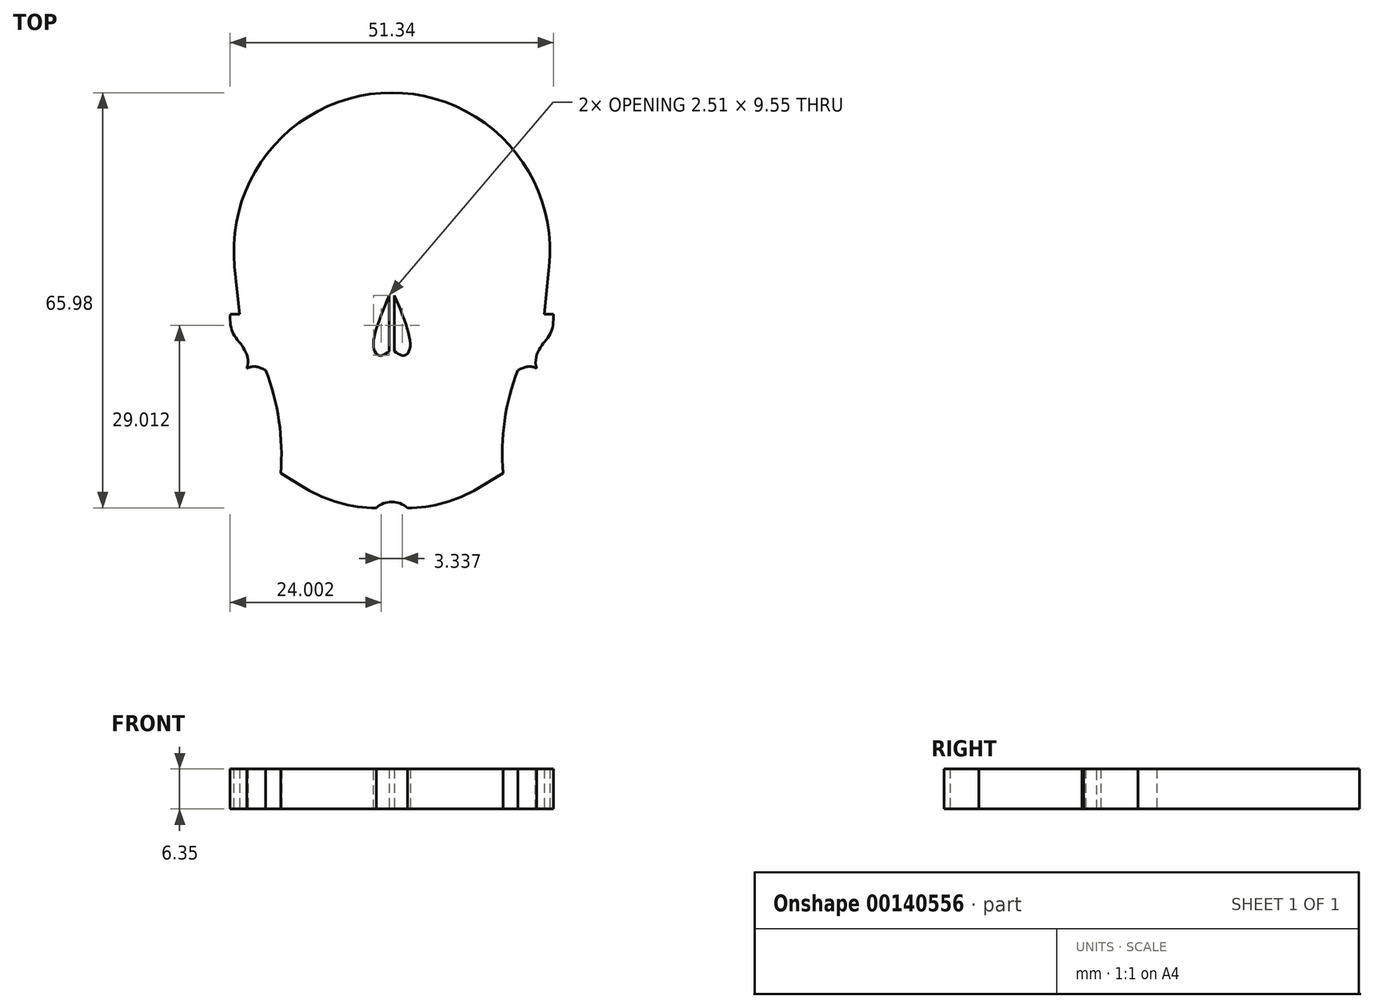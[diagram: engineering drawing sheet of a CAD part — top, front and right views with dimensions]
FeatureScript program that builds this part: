
annotation { "Feature Type Name" : "Feature", "Feature Type Description" : "" }
export const myFeature = defineFeature(function(context is Context, id is Id, definition is map)
    precondition{}
    {
        {
            var Q0;
            Q0=qCreatedBy(makeId("Top.planeOp"),FACE);
            var sketch = newSketch(context, id + "F0", { "sketchPlane" : qUnion([Q0])});
            skLineSegment(sketch, "E0", {"start": v(-25.4, 63.5) * mm, "end": v(25.4, 63.5) * mm});
            skArc(sketch, "E1", {"start": v(24.97, 27.94) * mm, "mid": v(0, 55.58) * mm, "end": v(-24.97, 27.94) * mm});
            skLineSegment(sketch, "E2", {"start": v(24.97, 27.94) * mm, "end": v(24.2, 20.36) * mm});
            skLineSegment(sketch, "E3", {"start": v(-24.97, 27.94) * mm, "end": v(-24.2, 20.36) * mm});
            skLineSegment(sketch, "E4", {"start": v(-24.2, 20.36) * mm, "end": v(-25.65, 20.36) * mm});
            skFitSpline(sketch, "E5", {"points": [v(-25.65, 20.36) * mm, v(-25.23, 17.4) * mm, v(-23.6, 15.1) * mm, v(-23.02, 11.75) * mm], "startDerivative": vector(-0.54, -10.14) * mm, "endDerivative": vector(-3.64, -10.9) * mm});
            skFitSpline(sketch, "E6", {"points": [v(-23.02, 11.75) * mm, v(-21.45, 12.02) * mm, v(-15.52, 10.2) * mm, v(-12.1, 12.07) * mm, v(-11.03, 11.75) * mm], "startDerivative": vector(6.84, 3.43) * mm, "endDerivative": vector(6.22, -4.3) * mm});
            skLineSegment(sketch, "E7", {"start": v(-0.41, 23.39) * mm, "end": v(-0.41, 14.49) * mm});
            skFitSpline(sketch, "E8", {"points": [v(-0.41, 23.39) * mm, v(-2.9, 15.1) * mm, v(-1.91, 13.82) * mm, v(-0.41, 14.49) * mm], "startDerivative": vector(-7.67, -18.3) * mm, "endDerivative": vector(6.65, 4.7) * mm});
            skFitSpline(sketch, "E9.MirrorCS", {"points": [v(0.41, 23.39) * mm, v(2.9, 15.1) * mm, v(1.91, 13.82) * mm, v(0.41, 14.49) * mm], "startDerivative": vector(7.67, -18.3) * mm, "endDerivative": vector(-6.65, 4.7) * mm});
            skLineSegment(sketch, "E10.MirrorCS", {"start": v(0.41, 23.39) * mm, "end": v(0.41, 14.49) * mm});
            skFitSpline(sketch, "E11.MirrorCS", {"points": [v(25.65, 20.36) * mm, v(25.23, 17.4) * mm, v(23.6, 15.1) * mm, v(23.02, 11.75) * mm], "startDerivative": vector(0.54, -10.14) * mm, "endDerivative": vector(3.64, -10.9) * mm});
            skFitSpline(sketch, "E12.MirrorCS", {"points": [v(23.02, 11.75) * mm, v(21.45, 12.02) * mm, v(15.52, 10.2) * mm, v(12.1, 12.07) * mm, v(11.03, 11.75) * mm], "startDerivative": vector(-6.84, 3.43) * mm, "endDerivative": vector(-6.22, -4.3) * mm});
            skLineSegment(sketch, "E13.MirrorCS", {"start": v(24.2, 20.36) * mm, "end": v(25.65, 20.36) * mm});
            skArc(sketch, "E14", {"start": v(-17.65, -4.87) * mm, "mid": v(-17.92, 3.45) * mm, "end": v(-20.04, 11.5) * mm});
            skLineSegment(sketch, "E15", {"start": v(-17.65, -4.87) * mm, "end": v(-13.68, -7.28) * mm});
            skArc(sketch, "E16", {"start": v(-13.68, -7.28) * mm, "mid": v(-8.3, -9.61) * mm, "end": v(-2.48, -10.4) * mm});
            skArc(sketch, "E17.MirrorCS", {"start": v(17.65, -4.87) * mm, "mid": v(17.92, 3.45) * mm, "end": v(20.04, 11.5) * mm});
            skLineSegment(sketch, "E18.MirrorCS", {"start": v(17.65, -4.87) * mm, "end": v(13.68, -7.28) * mm});
            skArc(sketch, "E19.MirrorCS", {"start": v(13.68, -7.28) * mm, "mid": v(8.3, -9.61) * mm, "end": v(2.48, -10.4) * mm});
            skArc(sketch, "E20", {"start": v(2.48, -10.4) * mm, "mid": v(0, -9.44) * mm, "end": v(-2.48, -10.4) * mm});
            skSolve(sketch);
        }
        {
            var Q0;
            Q0 = qSketchRegion(id + "F0", true);
            extrude(context, id + "F1", {"entities" : qUnion([Q0]), "depth" : 6.35 * mm});
        }
    });
